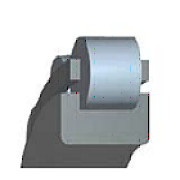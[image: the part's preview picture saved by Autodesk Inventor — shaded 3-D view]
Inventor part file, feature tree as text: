
AUTODESK INVENTOR PART (.ipt)
format: ipt  version: 2020.2 (Build 242310000, 310)  size: 168,448 bytes
history: native  units: mm (DEFAULTED — no unit token found)
features: sketch x1
ambient origin geometry x8: Origin, YZ Plane, XZ Plane, XY Plane, X Axis, Y Axis, Z Axis, Center Point
bodies: Solid1 (feature_tree), Body (feature_tree)
feature tree (1):
  sketch  "Sketch"  dims[d0=5.0mm d1=5.0mm d2=8.666667mm d3=16.0mm d4=90.0deg d5=0.275mm d6=0.0mm d7=0.0mm d8=0.0mm d9=0.0mm d10=0.0mm]
